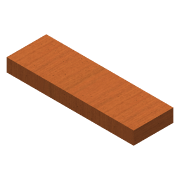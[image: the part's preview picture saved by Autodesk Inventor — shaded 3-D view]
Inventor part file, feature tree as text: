
AUTODESK INVENTOR PART (.ipt)
format: ipt  version: 2016 SP2 (Build 200236200, 236)  size: 86,016 bytes
history: native  units: in
note: dims shown in document units (in); Inventor stores cm internally (conversion verified against a paired STEP export)
features: extrude x1, sketch x1
ambient origin geometry x8: Origin, YZ Plane, XZ Plane, XY Plane, X Axis, Y Axis, Z Axis, Center Point
bodies: Solid1 (feature_tree)
feature tree (2):
  extrude  "Extrusion1"  Depth=1.4961in
  sketch  "Sketch1"  dims[d0=14.3701in d1=1.4961in d2=90.0deg d3=4.4882in d4=0.0in]
